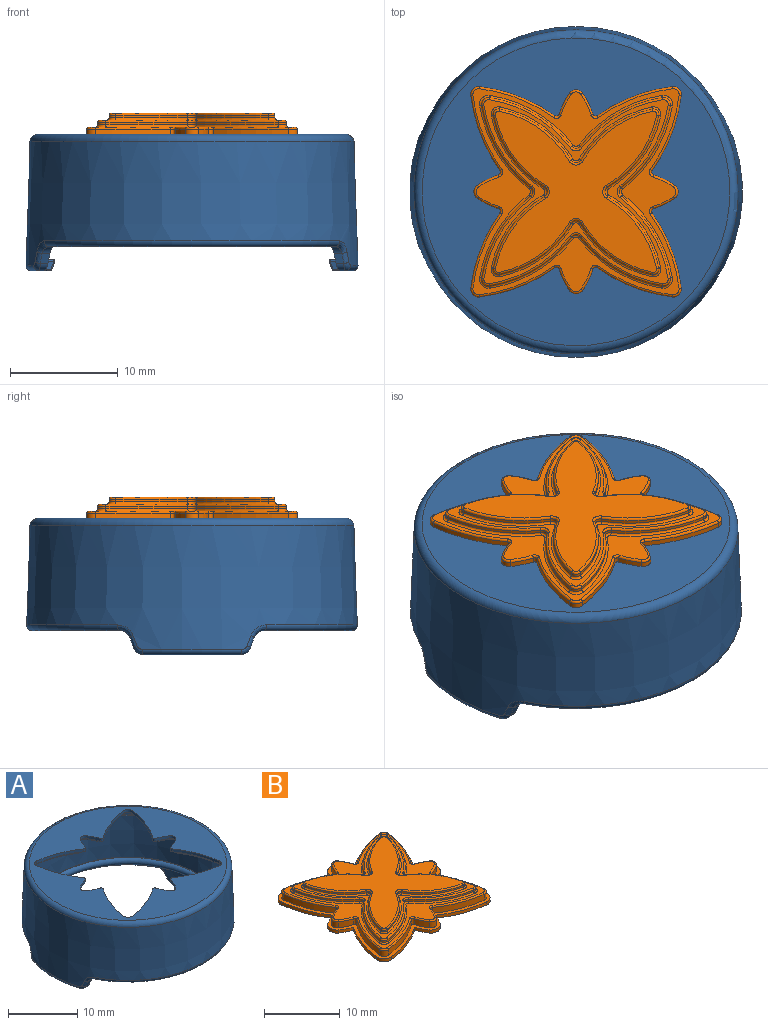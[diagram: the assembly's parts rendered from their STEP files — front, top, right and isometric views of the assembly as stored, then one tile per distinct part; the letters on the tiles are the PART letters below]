
ASSEMBLY  parts=2 mates=1
PART A: 150 faces, bbox 33.4x33.2x17.4 mm
  f0: plane 17.7x5.89mm, normal (0,0,-1), area 57.3mm2, adj f91,f125,f126,f127,f128,f129
  f1: plane 17.7x5.89mm, normal (0,0,-1), area 57.3mm2, adj f91,f131,f132,f133,f134,f135
  f2: plane 17.7x5.89mm, normal (0,0,-1), area 57.3mm2, adj f91,f137,f138,f139,f140,f141
  f3: plane 28.52x28.52mm, normal (0,0,1), area 337.1mm2, adj f15,f93,f94,f95,f96,f97,f98,f99
  f4: plane 17.7x5.89mm, normal (0,0,-1), area 57.3mm2, adj f91,f143,f144,f145,f146,f147
  f5: cone r=14.12mm half-angle=2deg, axis (0,0,-1), area 59.9mm2, adj f6,f7,f9,f10,f11,f12,f13,f14
  f6: plane 26.46x8.13mm, normal (0,0,-1), area 15.4mm2, adj f5,f17,f20,f79
  f7: plane 26.46x8.13mm, normal (0,0,-1), area 15.4mm2, adj f5,f16,f21,f80
  f8: cone r=15.12mm half-angle=2deg, axis (0,0,-1), area 926.8mm2, adj f15,f72,f73,f74,f75,f76,f77,f78
  f9: plane 0.94x0.89mm, normal (0,-0.94,-0.34), area 0.7mm2, adj f5,f20,f22,f75
  f10: plane 0.94x0.89mm, normal (0,0.94,-0.34), area 0.7mm2, adj f5,f21,f23,f76
  f11: plane 9x1.24mm, normal (0,0,-1), area 4.3mm2, adj f5,f22,f23,f25,f42,f65,f72
  f12: plane 0.94x0.89mm, normal (0,-0.94,-0.34), area 0.7mm2, adj f5,f17,f19,f83
  f13: plane 0.94x0.89mm, normal (0,0.94,-0.34), area 0.7mm2, adj f5,f16,f18,f84
  f14: plane 9x1.24mm, normal (0,0,-1), area 4.3mm2, adj f5,f18,f19,f31,f47,f64,f87
  f15: torus R=14.26mm, axis (0,0,1), area 106.6mm2, adj f3,f8
  f16: cylinder r=1mm len=1.2mm, axis (1,0,0), area 0.8mm2, adj f5,f7,f13,f82
  f17: cylinder r=1mm len=1.2mm, axis (1,0,0), area 0.8mm2, adj f5,f6,f12,f81
  f18: cylinder r=1mm len=0.94mm, axis (1,0,0), area 0.7mm2, adj f5,f13,f14,f86
  f19: cylinder r=1mm len=0.94mm, axis (1,0,0), area 0.7mm2, adj f5,f12,f14,f85
  f20: cylinder r=1mm len=1.2mm, axis (-1,0,0), area 0.8mm2, adj f5,f6,f9,f77
  f21: cylinder r=1mm len=1.2mm, axis (-1,0,0), area 0.8mm2, adj f5,f7,f10,f78
  f22: cylinder r=1mm len=0.94mm, axis (-1,0,0), area 0.7mm2, adj f5,f9,f11,f73
  f23: cylinder r=1mm len=0.94mm, axis (-1,0,0), area 0.7mm2, adj f5,f10,f11,f74
  f24: plane 7.08x1.39mm, normal (0,0,1), area 6.7mm2, adj f34,f35,f36,f68
  f25: plane 7.53x1.37mm, normal (0,0,-1), area 6.3mm2, adj f11,f39,f42,f45,f71
  f26: cone r=13.04mm half-angle=20.9deg, axis (0,0,-1), area 5.3mm2, adj f35,f40,f41,f45
  f27: plane 0.98x0.75mm, normal (0.26,-0.97,0), area 0.6mm2, adj f34,f39,f40,f70
  f28: plane 0.98x0.75mm, normal (0.26,0.97,0), area 0.6mm2, adj f36,f41,f42,f66
  f29: plane 7.08x1.39mm, normal (0,0,1), area 6.7mm2, adj f52,f53,f57,f61
  f30: cone r=13.04mm half-angle=20.9deg, axis (0,0,-1), area 5.3mm2, adj f48,f51,f54,f57
  f31: plane 7.53x1.37mm, normal (0,0,-1), area 6.3mm2, adj f14,f46,f47,f48,f58
  f32: plane 0.98x0.75mm, normal (-0.26,0.97,0), area 0.6mm2, adj f46,f51,f52,f59
  f33: plane 0.98x0.75mm, normal (-0.26,-0.97,0), area 0.6mm2, adj f47,f53,f54,f63
  f34: cylinder r=0.15mm len=0.99mm, axis (0.97,0.26,0), area 0.2mm2, adj f24,f27,f37,f69
  f35: torus R=13.26mm, axis (0,0,1), area 1.9mm2, adj f24,f26,f37,f38
  f36: cylinder r=0.15mm len=0.99mm, axis (-0.97,0.26,0), area 0.2mm2, adj f24,f28,f38,f67
  f37: sphere r=0.15mm, area 0.1mm2, adj f34,f35,f40
  f38: sphere r=0.15mm, area 0mm2, adj f35,f36,f41
  f39: cylinder r=0.15mm len=0.75mm, axis (-0.97,-0.26,0), area 0.2mm2, adj f25,f27,f43,f71
  f40: bspline ~10.55x4mm, area 0.2mm2, adj f26,f27,f37,f43
  f41: bspline ~10.55x4mm, area 0.2mm2, adj f26,f28,f38,f44
  f42: cylinder r=0.15mm len=0.9mm, axis (0.97,-0.26,0), area 0.2mm2, adj f11,f25,f28,f44,f65
  f43: sphere r=0.15mm, area 0mm2, adj f39,f40,f45
  f44: sphere r=0.15mm, area 0mm2, adj f41,f42,f45
  f45: torus R=13.55mm, axis (0,0,-1), area 1.2mm2, adj f25,f26,f43,f44
  f46: cylinder r=0.15mm len=0.75mm, axis (-0.97,-0.26,0), area 0.2mm2, adj f31,f32,f49,f58
  f47: cylinder r=0.15mm len=0.9mm, axis (0.97,-0.26,0), area 0.2mm2, adj f14,f31,f33,f50,f64
  f48: torus R=13.55mm, axis (0,0,-1), area 1.2mm2, adj f30,f31,f49,f50
  f49: sphere r=0.15mm, area 0mm2, adj f46,f48,f51
  f50: sphere r=0.15mm, area 0mm2, adj f47,f48,f54
  f51: bspline ~10.55x4mm, area 0.2mm2, adj f30,f32,f49,f55
  f52: cylinder r=0.15mm len=0.99mm, axis (0.97,0.26,0), area 0.2mm2, adj f29,f32,f55,f60
  f53: cylinder r=0.15mm len=0.99mm, axis (-0.97,0.26,0), area 0.2mm2, adj f29,f33,f56,f62
  f54: bspline ~10.55x4mm, area 0.2mm2, adj f30,f33,f50,f56
  f55: sphere r=0.15mm, area 0.1mm2, adj f51,f52,f57
  f56: sphere r=0.15mm, area 0mm2, adj f53,f54,f57
  f57: torus R=13.26mm, axis (0,0,1), area 1.9mm2, adj f29,f30,f55,f56
  f58: bspline ~0.35x0.34mm, area 0mm2, adj f5,f31,f46,f59
  f59: bspline ~3.76x0.27mm, area 0.2mm2, adj f5,f32,f58,f60
  f60: bspline ~0.37x0.32mm, area 0.1mm2, adj f5,f52,f59,f61
  f61: torus R=14.23mm, axis (0,0,1), area 1.7mm2, adj f5,f29,f60,f62
  f62: bspline ~0.37x0.34mm, area 0.1mm2, adj f5,f53,f61,f63
  f63: bspline ~3.76x0.27mm, area 0.2mm2, adj f5,f33,f62,f64
  f64: bspline ~0.34x0.33mm, area 0mm2, adj f5,f14,f47,f63
  f65: bspline ~0.34x0.33mm, area 0mm2, adj f5,f11,f42,f66
  f66: bspline ~3.76x0.27mm, area 0.2mm2, adj f5,f28,f65,f67
  f67: bspline ~0.37x0.34mm, area 0.1mm2, adj f5,f36,f66,f68
  f68: torus R=14.23mm, axis (0,0,1), area 1.7mm2, adj f5,f24,f67,f69
  f69: bspline ~0.37x0.32mm, area 0.1mm2, adj f5,f34,f68,f70
  f70: bspline ~3.76x0.27mm, area 0.2mm2, adj f5,f27,f69,f71
  f71: bspline ~0.35x0.34mm, area 0mm2, adj f5,f25,f39,f70
  f72: torus R=14.91mm, axis (0,0,-1), area 7.5mm2, adj f8,f11,f73,f74
  f73: bspline ~1.22x0.96mm, area 0.7mm2, adj f8,f22,f72,f75
  f74: bspline ~1.22x0.96mm, area 0.7mm2, adj f8,f23,f72,f76
  f75: bspline ~8.52x3.4mm, area 0.6mm2, adj f8,f9,f73,f77
  f76: bspline ~8.52x3.4mm, area 0.6mm2, adj f8,f10,f74,f78
  f77: bspline ~1.92x1.38mm, area 1.1mm2, adj f8,f20,f75,f79
  f78: bspline ~1.87x1.34mm, area 1.1mm2, adj f8,f21,f76,f80
  f79: torus R=14.83mm, axis (0,0,1), area 26.8mm2, adj f6,f8,f77,f81
  f80: torus R=14.83mm, axis (0,0,1), area 26.8mm2, adj f7,f8,f78,f82
  f81: bspline ~1.87x1.34mm, area 1.1mm2, adj f8,f17,f79,f83
  f82: bspline ~1.92x1.38mm, area 1.1mm2, adj f8,f16,f80,f84
  f83: bspline ~8.52x3.4mm, area 0.6mm2, adj f8,f12,f81,f85
  f84: bspline ~8.52x3.4mm, area 0.6mm2, adj f8,f13,f82,f86
  f85: bspline ~1.22x0.96mm, area 0.7mm2, adj f8,f19,f83,f87
  f86: bspline ~1.22x0.96mm, area 0.7mm2, adj f8,f18,f84,f87
  f87: torus R=14.91mm, axis (0,0,-1), area 7.5mm2, adj f8,f14,f85,f86
  f88: plane 28.67x28.67mm, normal (0,0,-1), area 11mm2, adj f5,f90
  f89: plane 28.6x28.6mm, normal (0,0,1), area 7.6mm2, adj f90,f92
  f90: torus R=14.21mm, axis (0,0,-1), area 150.5mm2, adj f88,f89
  f91: torus R=13.54mm, axis (0,0,1), area 66.8mm2, adj f0,f1,f2,f4,f92,f130,f136,f142
  f92: cone r=14.12mm half-angle=2deg, axis (0,0,-1), area 670.9mm2, adj f89,f91
  f93: cylinder r=0.25mm len=0.5mm, axis (0,0,-1), area 0.2mm2, adj f3,f94,f124,f149
  f94: cylinder r=15mm len=6.96mm, axis (0,0,-1), area 3.8mm2, adj f3,f93,f95,f149
  f95: cylinder r=0.75mm len=0.84mm, axis (0,0,-1), area 0.7mm2, adj f3,f94,f96,f149
  f96: cylinder r=15mm len=6.96mm, axis (0,0,-1), area 3.8mm2, adj f3,f95,f97,f149
  f97: cylinder r=0.25mm len=0.5mm, axis (0,0,-1), area 0.2mm2, adj f3,f96,f98,f149
  f98: cylinder r=7mm len=1.97mm, axis (0,0,-1), area 1.1mm2, adj f3,f97,f99,f149
  f99: cylinder r=0.75mm len=1.23mm, axis (0,0,-1), area 0.7mm2, adj f3,f98,f100,f149
  f100: cylinder r=7mm len=1.97mm, axis (0,0,-1), area 1.1mm2, adj f3,f99,f101,f149
  f101: cylinder r=0.25mm len=0.5mm, axis (0,0,-1), area 0.2mm2, adj f3,f100,f102,f149
  f102: cylinder r=15mm len=6.96mm, axis (0,0,-1), area 3.8mm2, adj f3,f101,f103,f149
  f103: cylinder r=0.75mm len=0.84mm, axis (0,0,-1), area 0.7mm2, adj f3,f102,f104,f149
  f104: cylinder r=15mm len=6.96mm, axis (0,0,-1), area 3.8mm2, adj f3,f103,f105,f149
  f105: cylinder r=0.25mm len=0.5mm, axis (0,0,-1), area 0.2mm2, adj f3,f104,f106,f149
  f106: cylinder r=7mm len=1.97mm, axis (0,0,-1), area 1.1mm2, adj f3,f105,f107,f149
  f107: cylinder r=0.75mm len=1.23mm, axis (0,0,-1), area 0.7mm2, adj f3,f106,f108,f149
  f108: cylinder r=7mm len=1.97mm, axis (0,0,-1), area 1.1mm2, adj f3,f107,f109,f149
  f109: cylinder r=0.25mm len=0.5mm, axis (0,0,-1), area 0.2mm2, adj f3,f108,f110,f149
  f110: cylinder r=15mm len=6.96mm, axis (0,0,-1), area 3.8mm2, adj f3,f109,f111,f149
  f111: cylinder r=0.75mm len=0.84mm, axis (0,0,-1), area 0.7mm2, adj f3,f110,f112,f149
  f112: cylinder r=15mm len=6.96mm, axis (0,0,-1), area 3.8mm2, adj f3,f111,f113,f149
  f113: cylinder r=0.25mm len=0.5mm, axis (0,0,-1), area 0.2mm2, adj f3,f112,f114,f149
  f114: cylinder r=7mm len=1.97mm, axis (0,0,-1), area 1.1mm2, adj f3,f113,f115,f149
  f115: cylinder r=0.75mm len=1.23mm, axis (0,0,-1), area 0.7mm2, adj f3,f114,f116,f149
  f116: cylinder r=7mm len=1.97mm, axis (0,0,-1), area 1.1mm2, adj f3,f115,f117,f149
  f117: cylinder r=0.25mm len=0.5mm, axis (0,0,-1), area 0.2mm2, adj f3,f116,f118,f149
  f118: cylinder r=15mm len=6.96mm, axis (0,0,-1), area 3.8mm2, adj f3,f117,f119,f149
  f119: cylinder r=0.75mm len=0.84mm, axis (0,0,-1), area 0.7mm2, adj f3,f118,f120,f149
  f120: cylinder r=15mm len=6.96mm, axis (0,0,-1), area 3.8mm2, adj f3,f119,f121,f149
  f121: cylinder r=0.25mm len=0.5mm, axis (0,0,-1), area 0.2mm2, adj f3,f120,f122,f149
  f122: cylinder r=7mm len=1.97mm, axis (0,0,-1), area 1.1mm2, adj f3,f121,f123,f149
  f123: cylinder r=0.75mm len=1.23mm, axis (0,0,-1), area 0.7mm2, adj f3,f122,f124,f149
  f124: cylinder r=7mm len=1.97mm, axis (0,0,-1), area 1.1mm2, adj f3,f93,f123,f149
  f125: cylinder r=15.5mm len=6.91mm, axis (0,0,-1), area 3.7mm2, adj f0,f126,f148,f149
  f126: cylinder r=7.5mm len=1.78mm, axis (0,0,-1), area 1mm2, adj f0,f125,f127,f149
  f127: cylinder r=1.25mm len=2.05mm, axis (0,0,-1), area 1.2mm2, adj f0,f126,f128,f149
  f128: cylinder r=7.5mm len=1.78mm, axis (0,0,-1), area 1mm2, adj f0,f127,f129,f149
  f129: cylinder r=15.5mm len=6.91mm, axis (0,0,-1), area 3.7mm2, adj f0,f128,f130,f149
  f130: cylinder r=13.54mm len=1.39mm, axis (0,0,-1), area 1mm2, adj f91,f129,f131,f149
  f131: cylinder r=15.5mm len=6.91mm, axis (0,0,-1), area 3.7mm2, adj f1,f130,f132,f149
  f132: cylinder r=7.5mm len=1.78mm, axis (0,0,-1), area 1mm2, adj f1,f131,f133,f149
  f133: cylinder r=1.25mm len=2.05mm, axis (0,0,-1), area 1.2mm2, adj f1,f132,f134,f149
  f134: cylinder r=7.5mm len=1.78mm, axis (0,0,-1), area 1mm2, adj f1,f133,f135,f149
  f135: cylinder r=15.5mm len=6.91mm, axis (0,0,-1), area 3.7mm2, adj f1,f134,f136,f149
  f136: cylinder r=13.54mm len=1.39mm, axis (0,0,-1), area 1mm2, adj f91,f135,f137,f149
  f137: cylinder r=15.5mm len=6.91mm, axis (0,0,-1), area 3.7mm2, adj f2,f136,f138,f149
  f138: cylinder r=7.5mm len=1.78mm, axis (0,0,-1), area 1mm2, adj f2,f137,f139,f149
  f139: cylinder r=1.25mm len=2.05mm, axis (0,0,-1), area 1.2mm2, adj f2,f138,f140,f149
  f140: cylinder r=7.5mm len=1.78mm, axis (0,0,-1), area 1mm2, adj f2,f139,f141,f149
  f141: cylinder r=15.5mm len=6.91mm, axis (0,0,-1), area 3.7mm2, adj f2,f140,f142,f149
  f142: cylinder r=13.54mm len=1.39mm, axis (0,0,-1), area 1mm2, adj f91,f141,f143,f149
  f143: cylinder r=15.5mm len=6.91mm, axis (0,0,-1), area 3.7mm2, adj f4,f142,f144,f149
  f144: cylinder r=7.5mm len=1.78mm, axis (0,0,-1), area 1mm2, adj f4,f143,f145,f149
  f145: cylinder r=1.25mm len=2.05mm, axis (0,0,-1), area 1.2mm2, adj f4,f144,f146,f149
  f146: cylinder r=7.5mm len=1.78mm, axis (0,0,-1), area 1mm2, adj f4,f145,f147,f149
  f147: cylinder r=15.5mm len=6.91mm, axis (0,0,-1), area 3.7mm2, adj f4,f146,f148,f149
  f148: cylinder r=13.54mm len=1.39mm, axis (0,0,-1), area 1mm2, adj f91,f125,f147,f149
  f149: plane 20.49x20.49mm, normal (0,0,-1), area 44.6mm2, adj f93,f94,f95,f96,f97,f98,f99,f100
PART B: 238 faces, bbox 21.9x21.9x3.2 mm
  f0: cylinder r=1.25mm len=2.05mm, axis (0,0,-1), area 1.2mm2, adj f1,f23,f24,f25
  f1: cylinder r=7.5mm len=1.78mm, axis (0,0,-1), area 1mm2, adj f0,f2,f24,f25
  f2: cylinder r=15.5mm len=6.91mm, axis (0,0,-1), area 3.7mm2, adj f1,f3,f24,f25
  f3: cylinder r=1.25mm len=1.4mm, axis (0,0,-1), area 1.1mm2, adj f2,f4,f24,f25
  f4: cylinder r=15.5mm len=6.91mm, axis (0,0,-1), area 3.7mm2, adj f3,f5,f24,f25
  f5: cylinder r=7.5mm len=1.78mm, axis (0,0,-1), area 1mm2, adj f4,f6,f24,f25
  f6: cylinder r=1.25mm len=2.05mm, axis (0,0,-1), area 1.2mm2, adj f5,f7,f24,f25
  f7: cylinder r=7.5mm len=1.78mm, axis (0,0,-1), area 1mm2, adj f6,f8,f24,f25
  f8: cylinder r=15.5mm len=6.91mm, axis (0,0,-1), area 3.7mm2, adj f7,f9,f24,f25
  f9: cylinder r=1.25mm len=1.4mm, axis (0,0,-1), area 1.1mm2, adj f8,f10,f24,f25
  f10: cylinder r=15.5mm len=6.91mm, axis (0,0,-1), area 3.7mm2, adj f9,f11,f24,f25
  f11: cylinder r=7.5mm len=1.78mm, axis (0,0,-1), area 1mm2, adj f10,f12,f24,f25
  f12: cylinder r=1.25mm len=2.05mm, axis (0,0,-1), area 1.2mm2, adj f11,f13,f24,f25
  f13: cylinder r=7.5mm len=1.78mm, axis (0,0,-1), area 1mm2, adj f12,f14,f24,f25
  f14: cylinder r=15.5mm len=6.91mm, axis (0,0,-1), area 3.7mm2, adj f13,f15,f24,f25
  f15: cylinder r=1.25mm len=1.4mm, axis (0,0,-1), area 1.1mm2, adj f14,f16,f24,f25
  f16: cylinder r=15.5mm len=6.91mm, axis (0,0,-1), area 3.7mm2, adj f15,f17,f24,f25
  f17: cylinder r=7.5mm len=1.78mm, axis (0,0,-1), area 1mm2, adj f16,f18,f24,f25
  f18: cylinder r=1.25mm len=2.05mm, axis (0,0,-1), area 1.2mm2, adj f17,f19,f24,f25
  f19: cylinder r=7.5mm len=1.78mm, axis (0,0,-1), area 1mm2, adj f18,f20,f24,f25
  f20: cylinder r=15.5mm len=6.91mm, axis (0,0,-1), area 3.7mm2, adj f19,f21,f24,f25
  f21: cylinder r=1.25mm len=1.4mm, axis (0,0,-1), area 1.1mm2, adj f20,f22,f24,f25
  f22: cylinder r=15.5mm len=6.91mm, axis (0,0,-1), area 3.7mm2, adj f21,f23,f24,f25
  f23: cylinder r=7.5mm len=1.78mm, axis (0,0,-1), area 1mm2, adj f0,f22,f24,f25
  f24: plane 20.51x20.51mm, normal (0,0,1), area 47mm2, adj f0,f1,f2,f3,f4,f5,f6,f7
  f25: plane 20.51x20.51mm, normal (0,0,-1), area 156.5mm2, adj f0,f1,f2,f3,f4,f5,f6,f7
  f26: cylinder r=0.25mm len=0.95mm, axis (0,0,-1), area 0.5mm2, adj f24,f27,f57,f95
  f27: cylinder r=15mm len=6.96mm, axis (0,0,-1), area 7.2mm2, adj f24,f26,f28,f93
  f28: cylinder r=0.75mm len=0.95mm, axis (0,0,-1), area 1.3mm2, adj f24,f27,f29,f94
  f29: cylinder r=15mm len=6.96mm, axis (0,0,-1), area 7.2mm2, adj f24,f28,f30,f96
  f30: cylinder r=0.25mm len=0.95mm, axis (0,0,-1), area 0.5mm2, adj f24,f29,f31,f98
  f31: cylinder r=7mm len=1.97mm, axis (0,0,-1), area 2.1mm2, adj f24,f30,f32,f100
  f32: cylinder r=0.75mm len=1.23mm, axis (0,0,-1), area 1.4mm2, adj f24,f31,f33,f102
  f33: cylinder r=7mm len=1.97mm, axis (0,0,-1), area 2.1mm2, adj f24,f32,f34,f104
  f34: cylinder r=0.25mm len=0.95mm, axis (0,0,-1), area 0.5mm2, adj f24,f33,f35,f106
  f35: cylinder r=15mm len=6.96mm, axis (0,0,-1), area 7.2mm2, adj f24,f34,f36,f108
  f36: cylinder r=0.75mm len=0.95mm, axis (0,0,-1), area 1.3mm2, adj f24,f35,f37,f110
  f37: cylinder r=15mm len=6.96mm, axis (0,0,-1), area 7.2mm2, adj f24,f36,f38,f112
  f38: cylinder r=0.25mm len=0.95mm, axis (0,0,-1), area 0.5mm2, adj f24,f37,f39,f114
  f39: cylinder r=7mm len=1.97mm, axis (0,0,-1), area 2.1mm2, adj f24,f38,f40,f116
  f40: cylinder r=0.75mm len=1.23mm, axis (0,0,-1), area 1.4mm2, adj f24,f39,f41,f118
  f41: cylinder r=7mm len=1.97mm, axis (0,0,-1), area 2.1mm2, adj f24,f40,f42,f120
  f42: cylinder r=0.25mm len=0.95mm, axis (0,0,-1), area 0.5mm2, adj f24,f41,f43,f122
  f43: cylinder r=15mm len=6.96mm, axis (0,0,-1), area 7.2mm2, adj f24,f42,f44,f124
  f44: cylinder r=0.75mm len=0.95mm, axis (0,0,-1), area 1.3mm2, adj f24,f43,f45,f123
  f45: cylinder r=15mm len=6.96mm, axis (0,0,-1), area 7.2mm2, adj f24,f44,f46,f121
  f46: cylinder r=0.25mm len=0.95mm, axis (0,0,-1), area 0.5mm2, adj f24,f45,f47,f119
  f47: cylinder r=7mm len=1.97mm, axis (0,0,-1), area 2.1mm2, adj f24,f46,f48,f117
  f48: cylinder r=0.75mm len=1.23mm, axis (0,0,-1), area 1.4mm2, adj f24,f47,f49,f115
  f49: cylinder r=7mm len=1.97mm, axis (0,0,-1), area 2.1mm2, adj f24,f48,f50,f113
  f50: cylinder r=0.25mm len=0.95mm, axis (0,0,-1), area 0.5mm2, adj f24,f49,f51,f111
  f51: cylinder r=15mm len=6.96mm, axis (0,0,-1), area 7.2mm2, adj f24,f50,f52,f109
  f52: cylinder r=0.75mm len=0.95mm, axis (0,0,-1), area 1.3mm2, adj f24,f51,f53,f107
  f53: cylinder r=15mm len=6.96mm, axis (0,0,-1), area 7.2mm2, adj f24,f52,f54,f105
  f54: cylinder r=0.25mm len=0.95mm, axis (0,0,-1), area 0.5mm2, adj f24,f53,f55,f103
  f55: cylinder r=7mm len=1.97mm, axis (0,0,-1), area 2.1mm2, adj f24,f54,f56,f101
  f56: cylinder r=0.75mm len=1.23mm, axis (0,0,-1), area 1.4mm2, adj f24,f55,f57,f99
  f57: cylinder r=7mm len=1.97mm, axis (0,0,-1), area 2.1mm2, adj f24,f26,f56,f97
  f58: plane 19.11x19.11mm, normal (0,0,1), area 74.7mm2, adj f93,f94,f95,f96,f97,f98,f99,f100
  f59: cylinder r=0.5mm len=0.79mm, axis (0,0,-1), area 0.2mm2, adj f60,f74,f170,f186
  f60: cylinder r=12mm len=7.59mm, axis (0,0,-1), area 2.3mm2, adj f59,f61,f168,f184
  f61: cylinder r=0.65mm len=0.75mm, axis (0,0,-1), area 0.3mm2, adj f60,f62,f166,f182
  f62: cylinder r=12mm len=7.59mm, axis (0,0,-1), area 2.3mm2, adj f61,f63,f164,f180
  f63: cylinder r=0.5mm len=0.79mm, axis (0,0,-1), area 0.2mm2, adj f62,f64,f162,f178
  f64: cylinder r=12mm len=7.59mm, axis (0,0,-1), area 2.3mm2, adj f63,f65,f160,f176
  f65: cylinder r=0.65mm len=0.75mm, axis (0,0,-1), area 0.3mm2, adj f64,f66,f158,f174
  f66: cylinder r=12mm len=7.59mm, axis (0,0,-1), area 2.3mm2, adj f65,f67,f157,f173
  f67: cylinder r=0.5mm len=0.79mm, axis (0,0,-1), area 0.2mm2, adj f66,f68,f159,f175
  f68: cylinder r=12mm len=7.59mm, axis (0,0,-1), area 2.3mm2, adj f67,f69,f161,f177
  f69: cylinder r=0.65mm len=0.75mm, axis (0,0,-1), area 0.3mm2, adj f68,f70,f163,f179
  f70: cylinder r=12mm len=7.59mm, axis (0,0,-1), area 2.3mm2, adj f69,f71,f165,f181
  f71: cylinder r=0.5mm len=0.79mm, axis (0,0,-1), area 0.2mm2, adj f70,f72,f167,f183
  f72: cylinder r=12mm len=7.59mm, axis (0,0,-1), area 2.3mm2, adj f71,f73,f169,f185
  f73: cylinder r=0.65mm len=0.75mm, axis (0,0,-1), area 0.3mm2, adj f72,f74,f171,f187
  f74: cylinder r=12mm len=7.59mm, axis (0,0,-1), area 2.3mm2, adj f59,f73,f172,f188
  f75: plane 17.08x17.08mm, normal (0,0,1), area 31.1mm2, adj f141,f142,f143,f144,f145,f146,f147,f148
  f76: plane 14.94x14.94mm, normal (0,0,1), area 115mm2, adj f125,f126,f127,f128,f129,f130,f131,f132
  f77: cylinder r=10mm len=6.64mm, axis (0,0,-1), area 2.1mm2, adj f78,f92,f140,f156
  f78: cylinder r=0.5mm len=0.6mm, axis (0,0,-1), area 0.2mm2, adj f77,f79,f139,f155
  f79: cylinder r=10mm len=6.64mm, axis (0,0,-1), area 2.1mm2, adj f78,f80,f137,f153
  f80: cylinder r=0.5mm len=0.86mm, axis (0,0,-1), area 0.3mm2, adj f79,f81,f135,f151
  f81: cylinder r=10mm len=6.64mm, axis (0,0,-1), area 2.1mm2, adj f80,f82,f133,f149
  f82: cylinder r=0.5mm len=0.6mm, axis (0,0,-1), area 0.2mm2, adj f81,f83,f131,f147
  f83: cylinder r=10mm len=6.64mm, axis (0,0,-1), area 2.1mm2, adj f82,f84,f129,f145
  f84: cylinder r=0.5mm len=0.86mm, axis (0,0,-1), area 0.3mm2, adj f83,f85,f127,f143
  f85: cylinder r=10mm len=6.64mm, axis (0,0,-1), area 2.1mm2, adj f84,f86,f125,f141
  f86: cylinder r=0.5mm len=0.6mm, axis (0,0,-1), area 0.2mm2, adj f85,f87,f126,f142
  f87: cylinder r=10mm len=6.64mm, axis (0,0,-1), area 2.1mm2, adj f86,f88,f128,f144
  f88: cylinder r=0.5mm len=0.86mm, axis (0,0,-1), area 0.3mm2, adj f87,f89,f130,f146
  f89: cylinder r=10mm len=6.64mm, axis (0,0,-1), area 2.1mm2, adj f88,f90,f132,f148
  f90: cylinder r=0.5mm len=0.6mm, axis (0,0,-1), area 0.2mm2, adj f89,f91,f134,f150
  f91: cylinder r=10mm len=6.64mm, axis (0,0,-1), area 2.1mm2, adj f90,f92,f136,f152
  f92: cylinder r=0.5mm len=0.86mm, axis (0,0,-1), area 0.3mm2, adj f77,f91,f138,f154
  f93: torus R=14.8mm, axis (0,0,1), area 2.4mm2, adj f27,f58,f94,f95
  f94: torus R=0.55mm, axis (0,0,1), area 0.4mm2, adj f28,f58,f93,f96
  f95: torus R=0.45mm, axis (0,0,1), area 0.2mm2, adj f26,f58,f93,f97
  f96: torus R=14.8mm, axis (0,0,1), area 2.4mm2, adj f29,f58,f94,f98
  f97: torus R=6.8mm, axis (0,0,1), area 0.7mm2, adj f57,f58,f95,f99
  f98: torus R=0.45mm, axis (0,0,1), area 0.2mm2, adj f30,f58,f96,f100
  f99: torus R=0.55mm, axis (0,0,1), area 0.4mm2, adj f56,f58,f97,f101
  f100: torus R=6.8mm, axis (0,0,1), area 0.7mm2, adj f31,f58,f98,f102
  f101: torus R=6.8mm, axis (0,0,1), area 0.7mm2, adj f55,f58,f99,f103
  f102: torus R=0.55mm, axis (0,0,1), area 0.4mm2, adj f32,f58,f100,f104
  f103: torus R=0.45mm, axis (0,0,1), area 0.2mm2, adj f54,f58,f101,f105
  f104: torus R=6.8mm, axis (0,0,1), area 0.7mm2, adj f33,f58,f102,f106
  f105: torus R=14.8mm, axis (0,0,1), area 2.4mm2, adj f53,f58,f103,f107
  f106: torus R=0.45mm, axis (0,0,1), area 0.2mm2, adj f34,f58,f104,f108
  f107: torus R=0.55mm, axis (0,0,1), area 0.4mm2, adj f52,f58,f105,f109
  f108: torus R=14.8mm, axis (0,0,1), area 2.4mm2, adj f35,f58,f106,f110
  f109: torus R=14.8mm, axis (0,0,1), area 2.4mm2, adj f51,f58,f107,f111
  f110: torus R=0.55mm, axis (0,0,1), area 0.4mm2, adj f36,f58,f108,f112
  f111: torus R=0.45mm, axis (0,0,1), area 0.2mm2, adj f50,f58,f109,f113
  f112: torus R=14.8mm, axis (0,0,1), area 2.4mm2, adj f37,f58,f110,f114
  f113: torus R=6.8mm, axis (0,0,1), area 0.7mm2, adj f49,f58,f111,f115
  f114: torus R=0.45mm, axis (0,0,1), area 0.2mm2, adj f38,f58,f112,f116
  f115: torus R=0.55mm, axis (0,0,1), area 0.4mm2, adj f48,f58,f113,f117
  f116: torus R=6.8mm, axis (0,0,1), area 0.7mm2, adj f39,f58,f114,f118
  f117: torus R=6.8mm, axis (0,0,1), area 0.7mm2, adj f47,f58,f115,f119
  f118: torus R=0.55mm, axis (0,0,1), area 0.4mm2, adj f40,f58,f116,f120
  f119: torus R=0.45mm, axis (0,0,1), area 0.2mm2, adj f46,f58,f117,f121
  f120: torus R=6.8mm, axis (0,0,1), area 0.7mm2, adj f41,f58,f118,f122
  f121: torus R=14.8mm, axis (0,0,1), area 2.4mm2, adj f45,f58,f119,f123
  f122: torus R=0.45mm, axis (0,0,1), area 0.2mm2, adj f42,f58,f120,f124
  f123: torus R=0.55mm, axis (0,0,1), area 0.4mm2, adj f44,f58,f121,f124
  f124: torus R=14.8mm, axis (0,0,1), area 2.4mm2, adj f43,f58,f122,f123
  f125: torus R=9.8mm, axis (0,0,1), area 2.6mm2, adj f76,f85,f126,f127
  f126: torus R=0.3mm, axis (0,0,1), area 0.3mm2, adj f76,f86,f125,f128
  f127: torus R=0.7mm, axis (0,0,1), area 0.4mm2, adj f76,f84,f125,f129
  f128: torus R=9.8mm, axis (0,0,1), area 2.6mm2, adj f76,f87,f126,f130
  f129: torus R=9.8mm, axis (0,0,1), area 2.6mm2, adj f76,f83,f127,f131
  f130: torus R=0.7mm, axis (0,0,1), area 0.4mm2, adj f76,f88,f128,f132
  f131: torus R=0.3mm, axis (0,0,1), area 0.3mm2, adj f76,f82,f129,f133
  f132: torus R=9.8mm, axis (0,0,1), area 2.6mm2, adj f76,f89,f130,f134
  f133: torus R=9.8mm, axis (0,0,1), area 2.6mm2, adj f76,f81,f131,f135
  f134: torus R=0.3mm, axis (0,0,1), area 0.3mm2, adj f76,f90,f132,f136
  f135: torus R=0.7mm, axis (0,0,1), area 0.4mm2, adj f76,f80,f133,f137
  f136: torus R=9.8mm, axis (0,0,1), area 2.6mm2, adj f76,f91,f134,f138
  f137: torus R=9.8mm, axis (0,0,1), area 2.6mm2, adj f76,f79,f135,f139
  f138: torus R=0.7mm, axis (0,0,1), area 0.4mm2, adj f76,f92,f136,f140
  f139: torus R=0.3mm, axis (0,0,1), area 0.3mm2, adj f76,f78,f137,f140
  f140: torus R=9.8mm, axis (0,0,1), area 2.6mm2, adj f76,f77,f138,f139
  f141: torus R=10.2mm, axis (0,0,1), area 2.7mm2, adj f75,f85,f142,f143
  f142: torus R=0.7mm, axis (0,0,1), area 0.4mm2, adj f75,f86,f141,f144
  f143: torus R=0.3mm, axis (0,0,1), area 0.3mm2, adj f75,f84,f141,f145
  f144: torus R=10.2mm, axis (0,0,1), area 2.7mm2, adj f75,f87,f142,f146
  f145: torus R=10.2mm, axis (0,0,1), area 2.7mm2, adj f75,f83,f143,f147
  f146: torus R=0.3mm, axis (0,0,1), area 0.3mm2, adj f75,f88,f144,f148
  f147: torus R=0.7mm, axis (0,0,1), area 0.4mm2, adj f75,f82,f145,f149
  f148: torus R=10.2mm, axis (0,0,1), area 2.7mm2, adj f75,f89,f146,f150
  f149: torus R=10.2mm, axis (0,0,1), area 2.7mm2, adj f75,f81,f147,f151
  f150: torus R=0.7mm, axis (0,0,1), area 0.4mm2, adj f75,f90,f148,f152
  f151: torus R=0.3mm, axis (0,0,1), area 0.3mm2, adj f75,f80,f149,f153
  f152: torus R=10.2mm, axis (0,0,1), area 2.7mm2, adj f75,f91,f150,f154
  f153: torus R=10.2mm, axis (0,0,1), area 2.7mm2, adj f75,f79,f151,f155
  f154: torus R=0.3mm, axis (0,0,1), area 0.3mm2, adj f75,f92,f152,f156
  f155: torus R=0.7mm, axis (0,0,1), area 0.4mm2, adj f75,f78,f153,f156
  f156: torus R=10.2mm, axis (0,0,1), area 2.7mm2, adj f75,f77,f154,f155
  f157: torus R=11.8mm, axis (0,0,1), area 2.8mm2, adj f66,f75,f158,f159
  f158: torus R=0.45mm, axis (0,0,1), area 0.3mm2, adj f65,f75,f157,f160
  f159: torus R=0.7mm, axis (0,0,1), area 0.3mm2, adj f67,f75,f157,f161
  f160: torus R=11.8mm, axis (0,0,1), area 2.8mm2, adj f64,f75,f158,f162
  f161: torus R=11.8mm, axis (0,0,1), area 2.8mm2, adj f68,f75,f159,f163
  f162: torus R=0.7mm, axis (0,0,1), area 0.3mm2, adj f63,f75,f160,f164
  f163: torus R=0.45mm, axis (0,0,1), area 0.3mm2, adj f69,f75,f161,f165
  f164: torus R=11.8mm, axis (0,0,1), area 2.8mm2, adj f62,f75,f162,f166
  f165: torus R=11.8mm, axis (0,0,1), area 2.8mm2, adj f70,f75,f163,f167
  f166: torus R=0.45mm, axis (0,0,1), area 0.3mm2, adj f61,f75,f164,f168
  f167: torus R=0.7mm, axis (0,0,1), area 0.3mm2, adj f71,f75,f165,f169
  f168: torus R=11.8mm, axis (0,0,1), area 2.8mm2, adj f60,f75,f166,f170
  f169: torus R=11.8mm, axis (0,0,1), area 2.8mm2, adj f72,f75,f167,f171
  f170: torus R=0.7mm, axis (0,0,1), area 0.3mm2, adj f59,f75,f168,f172
  f171: torus R=0.45mm, axis (0,0,1), area 0.3mm2, adj f73,f75,f169,f172
  f172: torus R=11.8mm, axis (0,0,1), area 2.8mm2, adj f74,f75,f170,f171
  f173: torus R=12.2mm, axis (0,0,1), area 2.9mm2, adj f58,f66,f174,f175
  f174: torus R=0.85mm, axis (0,0,1), area 0.4mm2, adj f58,f65,f173,f176
  f175: torus R=0.3mm, axis (0,0,1), area 0.2mm2, adj f58,f67,f173,f177
  f176: torus R=12.2mm, axis (0,0,1), area 2.9mm2, adj f58,f64,f174,f178
  f177: torus R=12.2mm, axis (0,0,1), area 2.9mm2, adj f58,f68,f175,f179
  f178: torus R=0.3mm, axis (0,0,1), area 0.2mm2, adj f58,f63,f176,f180
  f179: torus R=0.85mm, axis (0,0,1), area 0.4mm2, adj f58,f69,f177,f181
  f180: torus R=12.2mm, axis (0,0,1), area 2.9mm2, adj f58,f62,f178,f182
  f181: torus R=12.2mm, axis (0,0,1), area 2.9mm2, adj f58,f70,f179,f183
  f182: torus R=0.85mm, axis (0,0,1), area 0.4mm2, adj f58,f61,f180,f184
  f183: torus R=0.3mm, axis (0,0,1), area 0.2mm2, adj f58,f71,f181,f185
  f184: torus R=12.2mm, axis (0,0,1), area 2.9mm2, adj f58,f60,f182,f186
  f185: torus R=12.2mm, axis (0,0,1), area 2.9mm2, adj f58,f72,f183,f187
  f186: torus R=0.3mm, axis (0,0,1), area 0.2mm2, adj f58,f59,f184,f188
  f187: torus R=0.85mm, axis (0,0,1), area 0.4mm2, adj f58,f73,f185,f188
  f188: torus R=12.2mm, axis (0,0,1), area 2.9mm2, adj f58,f74,f186,f187
  f189: cone r=0.5mm half-angle=2deg, axis (0,0,1), area 0.6mm2, adj f25,f190,f204,f205
  f190: cone r=12mm half-angle=2deg, axis (0,0,-1), area 5.9mm2, adj f25,f189,f191,f205
  f191: cone r=0.65mm half-angle=2deg, axis (0,0,-1), area 0.8mm2, adj f25,f190,f192,f205
  f192: cone r=12mm half-angle=2deg, axis (0,0,-1), area 5.9mm2, adj f25,f191,f193,f205
  f193: cone r=0.5mm half-angle=2deg, axis (0,0,1), area 0.6mm2, adj f25,f192,f194,f205
  f194: cone r=12mm half-angle=2deg, axis (0,0,-1), area 5.9mm2, adj f25,f193,f195,f205
  f195: cone r=0.65mm half-angle=2deg, axis (0,0,-1), area 0.8mm2, adj f25,f194,f196,f205
  f196: cone r=12mm half-angle=2deg, axis (0,0,-1), area 5.9mm2, adj f25,f195,f197,f205
  f197: cone r=0.5mm half-angle=2deg, axis (0,0,1), area 0.6mm2, adj f25,f196,f198,f205
  f198: cone r=12mm half-angle=2deg, axis (0,0,-1), area 5.9mm2, adj f25,f197,f199,f205
  f199: cone r=0.65mm half-angle=2deg, axis (0,0,-1), area 0.8mm2, adj f25,f198,f200,f205
  f200: cone r=12mm half-angle=2deg, axis (0,0,-1), area 5.9mm2, adj f25,f199,f201,f205
  f201: cone r=0.5mm half-angle=2deg, axis (0,0,1), area 0.6mm2, adj f25,f200,f202,f205
  f202: cone r=12mm half-angle=2deg, axis (0,0,-1), area 5.9mm2, adj f25,f201,f203,f205
  f203: cone r=0.65mm half-angle=2deg, axis (0,0,-1), area 0.8mm2, adj f25,f202,f204,f205
  f204: cone r=12mm half-angle=2deg, axis (0,0,-1), area 5.9mm2, adj f25,f189,f203,f205
  f205: plane 17.43x17.43mm, normal (0,0,-1), area 62.2mm2, adj f189,f190,f191,f192,f193,f194,f195,f196
  f206: plane 14.34x14.27mm, normal (0,0,-1), area 86.9mm2, adj f207,f208,f209,f210,f211,f212,f213,f214
  f207: cone r=1mm half-angle=2deg, axis (0,0,1), area 1.4mm2, adj f206,f208,f218,f219
  f208: cone r=9.5mm half-angle=2deg, axis (0,0,-1), area 5.1mm2, adj f206,f207,f209,f219
  f209: cylinder r=9.5mm len=6.26mm, axis (0,0,-1), area 5.1mm2, adj f206,f208,f210,f219
  f210: cylinder r=1mm len=1.73mm, axis (0,0,-1), area 1.4mm2, adj f206,f209,f211,f219
  f211: cylinder r=9.5mm len=6.31mm, axis (0,0,-1), area 5.2mm2, adj f206,f210,f212,f219
  f212: cylinder r=9.5mm len=6.31mm, axis (0,0,-1), area 5.2mm2, adj f206,f211,f213,f219
  f213: cylinder r=1mm len=1.73mm, axis (0,0,-1), area 1.4mm2, adj f206,f212,f214,f219
  f214: cylinder r=9.5mm len=6.31mm, axis (0,0,-1), area 5.2mm2, adj f206,f213,f215,f219
  f215: cylinder r=9.5mm len=6.31mm, axis (0,0,-1), area 5.2mm2, adj f206,f214,f216,f219
  f216: cylinder r=1mm len=1.73mm, axis (0,0,-1), area 1.4mm2, adj f206,f215,f217,f219
  f217: cylinder r=9.5mm len=6.26mm, axis (0,0,-1), area 5.1mm2, adj f206,f216,f218,f219
  f218: cone r=9.5mm half-angle=2deg, axis (0,0,-1), area 5.1mm2, adj f206,f207,f217,f219
  f219: plane 15.25x15.25mm, normal (0,0,-1), area 34.3mm2, adj f207,f208,f209,f210,f211,f212,f213,f214
  f220: cone r=10mm half-angle=2deg, axis (0,0,-1), area 5.4mm2, adj f205,f219,f221,f235
  f221: cone r=0.5mm half-angle=2deg, axis (0,0,-1), area 0.6mm2, adj f205,f219,f220,f222
  f222: cone r=10mm half-angle=2deg, axis (0,0,-1), area 5.4mm2, adj f205,f219,f221,f223
  f223: cone r=0.5mm half-angle=2deg, axis (0,0,1), area 0.7mm2, adj f205,f219,f222,f224
  f224: cone r=10mm half-angle=2deg, axis (0,0,-1), area 5.4mm2, adj f205,f219,f223,f225
  f225: cone r=0.5mm half-angle=2deg, axis (0,0,-1), area 0.6mm2, adj f205,f219,f224,f226
  f226: cone r=10mm half-angle=2deg, axis (0,0,-1), area 5.4mm2, adj f205,f219,f225,f227
  f227: cone r=0.5mm half-angle=2deg, axis (0,0,1), area 0.7mm2, adj f205,f219,f226,f228
  f228: cone r=10mm half-angle=2deg, axis (0,0,-1), area 5.4mm2, adj f205,f219,f227,f229
  f229: cone r=0.5mm half-angle=2deg, axis (0,0,-1), area 0.6mm2, adj f205,f219,f228,f230
  f230: cone r=10mm half-angle=2deg, axis (0,0,-1), area 5.4mm2, adj f205,f219,f229,f231
  f231: cone r=0.5mm half-angle=2deg, axis (0,0,1), area 0.7mm2, adj f205,f219,f230,f232
  f232: cone r=10mm half-angle=2deg, axis (0,0,-1), area 5.4mm2, adj f205,f219,f231,f233
  f233: cone r=0.5mm half-angle=2deg, axis (0,0,-1), area 0.6mm2, adj f205,f219,f232,f234
  f234: cone r=10mm half-angle=2deg, axis (0,0,-1), area 5.4mm2, adj f205,f219,f233,f235
  f235: cone r=0.5mm half-angle=2deg, axis (0,0,1), area 0.7mm2, adj f205,f219,f220,f234
  f236: cone r=1.25mm half-angle=5deg, axis (0,0,1), area 15.7mm2, adj f206,f237
  f237: plane 2.12x2.12mm, normal (0,0,-1), area 3.5mm2, adj f236
PLACE A at identity fixed
PLACE B t=(0,0,10.81)mm
MATE fastened B.f24 <-> A.f149  axis (0,0,1) through (9.42,-1.02,11.32)mm
